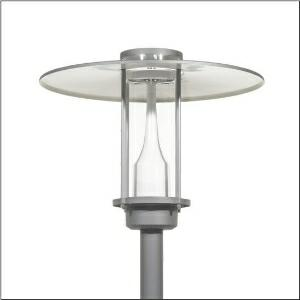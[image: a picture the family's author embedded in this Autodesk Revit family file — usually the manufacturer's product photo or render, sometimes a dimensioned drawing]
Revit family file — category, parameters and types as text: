
# Revit family: city-light_plus_iq___p1_0a_5xa5275nf14h_3f00
name_source: partatom
category: Lighting Fixtures
units: mm (PartAtom-declared; Revit-internal decimal feet)

## family parameters
Cut with Voids When Loaded = No
Host = Face
Light Source = No
Part Type = Normal
Room Calculation Point = No
Round Connector Dimension = Use Diameter
Shared = No

## types (1)
- --- (1 x LED, 1440 lm, 11.8 W, 2700K)
    Apparent Load = 12 VA
    CIE Flux Codes = 32 61 90 96 100
    Color Rendering = 70
    Color Temperature = 2700K
    Default Elevation = 1800 mm
    Description = City-Light Plus iQ, mast luminaire, Module 540 iQ-SR, primary light control with 3 zone facetted reflector, of plastic, silver coated, highly specular, structured, primary optical cover: cover, of PMMA, transparent, light distribution: P1.0a, light emission: direct distribution, primary light characteristic: strongly asymmetric, installation type: post-top, LED, High Power LED, rated luminous flux: 1.440lm, luminous efficacy: 122lm/W, light colour: 727, colour temperature: 2700K, control gear: iQ Street-Remote, control: pre-setting: logarithmic dimming characteristic, Street-Remote, Auto-Match, Temp-Guard, Lumen-Switch, Night-Set, Smart-Wire, Light-Fading, Desk-Remote (wireless, voltage-free reading and setting of iQ features in the workshop via application-optimized NFC function/RFID function), optimised constant luminous flux control (CLO 2.0), with terminal, 6-pole, max. 2.5mm², mains connection: 230..240V, AC, 50/60Hz, start of lifetime: 12W, end of service life: 12W, reduction: 6W, luminaire housing, upper part, of glass-fibre reinforced polyester, coated, Siteco® metallic grey (DB 702S), diameter: 750mm, height: 590mm, spigot size: d x l = 76 x 70mm (post-top) | with reducer (optional accessory) 60 x 70mm, mounting height: 3..5m, post-top mast mounting element, of diecast aluminium, coated, Siteco® metallic grey (DB 702S), Module 540 iQ-SR, traffic white (RAL 9016), equipment: standard, protection rating (complete): IP65, insulation class (complete): insulation class II (safety insulation), certification: CE, ENEC, VDE, packaging unit: 1 piece

Light Distribution: P1.0a
    Height = 590 mm
    Lamp = 1 x LED
    Lamp Light Flux = 1440 lm
    Lamp Power = 11.8 W
    Lamp count = 1
    Length = 750 mm
    Luminous efficacy = 122 lm/W
    Manufacturer = Siteco
    ModVariant = No
    Model = 5XA5275NF14H
    Number of Poles = 1
    OnlyDefault = Yes
    Power Factor = 1
    Product Name = City-Light Plus iQ | P1.0a
    Product group = mast luminaire | pylon top
    ProductGroupID = 6100
    Protection Class = Protection class II
    Protection Degree = IP 65
    RLX_Detail_Level = 1
    RLX_Emergency_Light_Flux = 0 lm
    RLX_Emergency_Type = 0
    RLX_Emergency_Type_DB = No
    RlxData = <blob elided: 60361 chars, md5=153e8f71>
    Socket = socket
    Standby Power = 0 W
    System Light Flux = 1440 lm
    System Power = 12 W
    Type Comments = factory setting: luminous flux: 100 % | dim-lin: 254 | 472 mA
    Type Image = l_1006456.jpg
    URL = http://relux.com
    VarID = @adj_153318
    Voltage = 0 V
    Weight = 0.00 kg
    Width = 0 mm  [stored 0 ft]

note: [stored X ft] marks values corroborated as IEEE doubles in the binary element streams (Revit-internal decimal feet)

## geometry (parser evidence)
native form markers: Blend x4, Sweep x11
no freeform markers — native parametric forms only
